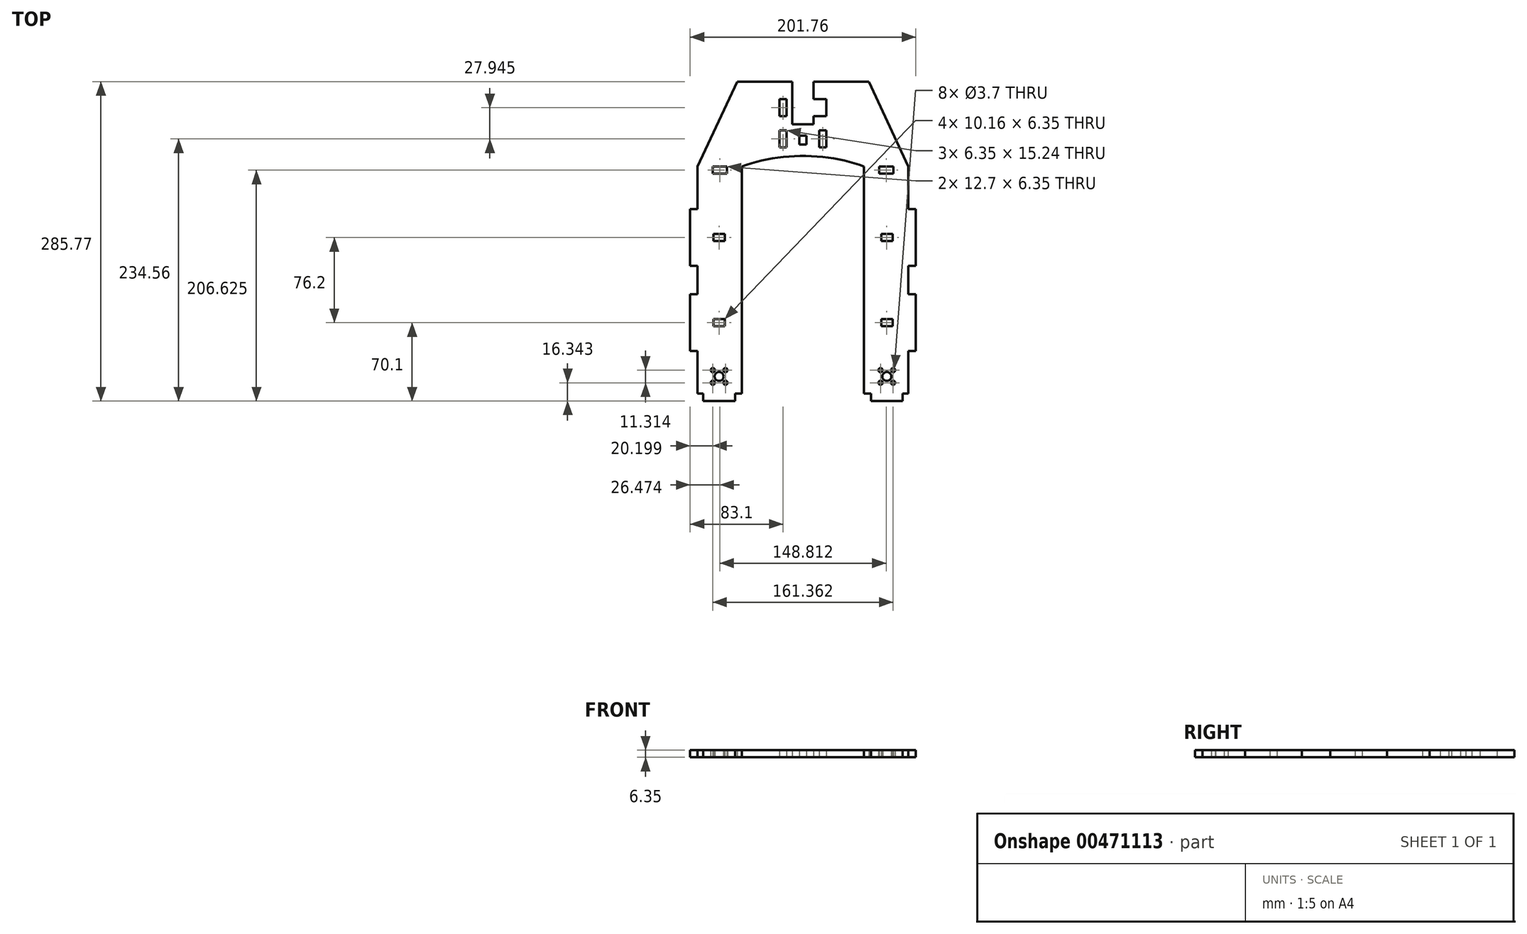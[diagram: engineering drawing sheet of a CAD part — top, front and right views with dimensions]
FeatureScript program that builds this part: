
annotation { "Feature Type Name" : "Feature", "Feature Type Description" : "" }
export const myFeature = defineFeature(function(context is Context, id is Id, definition is map)
    precondition{}
    {
        {
            var Q0;
            Q0=qCreatedBy(makeId("Top.planeOp"),FACE);
            var sketch = newSketch(context, id + "F0", { "sketchPlane" : qUnion([Q0])});
            skLineSegment(sketch, "E0", {"start": v(-60.85, 0) * mm, "end": v(-60.85, -6.6) * mm});
            skLineSegment(sketch, "E1", {"start": v(-60.85, -6.6) * mm, "end": v(-89.2, -6.6) * mm});
            skLineSegment(sketch, "E2", {"start": v(-89.2, -6.6) * mm, "end": v(-89.2, 0) * mm});
            skLineSegment(sketch, "E3", {"start": v(-89.2, 0) * mm, "end": v(-94.28, 0) * mm});
            skLineSegment(sketch, "E4", {"start": v(-60.85, 0) * mm, "end": v(-54.53, 0) * mm});
            skLineSegment(sketch, "E5", {"start": v(-94.28, 0) * mm, "end": v(-94.28, 38.1) * mm});
            skLineSegment(sketch, "E6", {"start": v(-54.53, 0) * mm, "end": v(-54.53, 203.2) * mm});
            skFitSpline(sketch, "E7", {"points": [v(-54.53, 203.2) * mm, v(54.53, 203.2) * mm], "startDerivative": vector(94.5, 38.1) * mm, "endDerivative": vector(94.5, -38.1) * mm});
            skLineSegment(sketch, "E8", {"start": v(-94.28, 38.1) * mm, "end": v(-100.88, 38.1) * mm});
            skLineSegment(sketch, "E9", {"start": v(-100.88, 38.1) * mm, "end": v(-100.88, 88.9) * mm});
            skLineSegment(sketch, "E10", {"start": v(-100.88, 88.9) * mm, "end": v(-94.28, 88.9) * mm});
            skLineSegment(sketch, "E11", {"start": v(-94.28, 165.1) * mm, "end": v(-100.88, 165.1) * mm});
            skLineSegment(sketch, "E12", {"start": v(-100.88, 165.1) * mm, "end": v(-100.88, 114.3) * mm});
            skLineSegment(sketch, "E13", {"start": v(-100.88, 114.3) * mm, "end": v(-94.28, 114.3) * mm});
            skLineSegment(sketch, "E14.trimOffspring", {"start": v(-94.28, 165.1) * mm, "end": v(-94.28, 203.2) * mm});
            skLineSegment(sketch, "E15.trimOffspring", {"start": v(-94.28, 88.9) * mm, "end": v(-94.28, 114.3) * mm});
            skCircle(sketch, "E16", {"center": v(-75.02, 15.4) * mm, "radius": 4 * mm});
            skCircle(sketch, "E17.1.0", {"center": v(-80.68, 9.74) * mm, "radius": 1.85 * mm});
            skCircle(sketch, "E18.1.3.0", {"center": v(-69.37, 9.74) * mm, "radius": 1.85 * mm});
            skCircle(sketch, "E18.1.5.0", {"center": v(-69.37, 21.06) * mm, "radius": 1.85 * mm});
            skCircle(sketch, "E18.1.7.0", {"center": v(-80.68, 21.06) * mm, "radius": 1.85 * mm});
            skLineSegment(sketch, "E19", {"start": v(-80.76, 203.2) * mm, "end": v(-80.76, 196.85) * mm});
            skLineSegment(sketch, "E20", {"start": v(-80.76, 196.85) * mm, "end": v(-68.06, 196.85) * mm});
            skLineSegment(sketch, "E21", {"start": v(-68.06, 196.85) * mm, "end": v(-68.06, 203.2) * mm});
            skLineSegment(sketch, "E22", {"start": v(-80.76, 203.2) * mm, "end": v(-68.06, 203.2) * mm});
            skLineSegment(sketch, "E23", {"start": v(0, 0) * mm, "end": v(0, 212.73) * mm, "construction": true});
            skLineSegment(sketch, "E24", {"start": v(-58.85, 279.17) * mm, "end": v(-9.53, 279.17) * mm});
            skLineSegment(sketch, "E25", {"start": v(-94.28, 203.2) * mm, "end": v(-58.85, 279.17) * mm});
            skLineSegment(sketch, "E26", {"start": v(-9.53, 279.17) * mm, "end": v(-9.53, 241.07) * mm});
            skLineSegment(sketch, "E27.MirrorCS", {"start": v(94.28, 203.2) * mm, "end": v(58.85, 279.17) * mm});
            skLineSegment(sketch, "E28.MirrorCS", {"start": v(9.53, 279.17) * mm, "end": v(9.53, 263.53) * mm});
            skLineSegment(sketch, "E29.MirrorCS", {"start": v(58.85, 279.17) * mm, "end": v(9.53, 279.17) * mm});
            skLineSegment(sketch, "E30.MirrorCS", {"start": v(80.76, 203.2) * mm, "end": v(80.76, 196.85) * mm});
            skCircle(sketch, "E31.MirrorC", {"center": v(69.37, 9.74) * mm, "radius": 1.85 * mm});
            skCircle(sketch, "E32.MirrorC", {"center": v(69.37, 21.06) * mm, "radius": 1.85 * mm});
            skLineSegment(sketch, "E33.MirrorCS", {"start": v(80.76, 196.85) * mm, "end": v(68.06, 196.85) * mm});
            skLineSegment(sketch, "E34.MirrorCS", {"start": v(100.88, 114.3) * mm, "end": v(94.28, 114.3) * mm});
            skCircle(sketch, "E35.MirrorC", {"center": v(75.02, 15.4) * mm, "radius": 4 * mm});
            skLineSegment(sketch, "E36.MirrorCS", {"start": v(89.2, -6.6) * mm, "end": v(89.2, 0) * mm});
            skLineSegment(sketch, "E37.MirrorCS", {"start": v(60.85, 0) * mm, "end": v(60.85, -6.6) * mm});
            skLineSegment(sketch, "E38.MirrorCS", {"start": v(60.85, 0) * mm, "end": v(54.53, 0) * mm});
            skLineSegment(sketch, "E39.MirrorCS", {"start": v(80.76, 203.2) * mm, "end": v(68.06, 203.2) * mm});
            skLineSegment(sketch, "E40.MirrorCS", {"start": v(94.28, 38.1) * mm, "end": v(100.88, 38.1) * mm});
            skLineSegment(sketch, "E41.MirrorCS", {"start": v(100.88, 88.9) * mm, "end": v(94.28, 88.9) * mm});
            skLineSegment(sketch, "E42.MirrorCS", {"start": v(94.28, 165.1) * mm, "end": v(100.88, 165.1) * mm});
            skLineSegment(sketch, "E43.MirrorCS", {"start": v(68.06, 196.85) * mm, "end": v(68.06, 203.2) * mm});
            skLineSegment(sketch, "E44.MirrorCS", {"start": v(89.2, 0) * mm, "end": v(94.28, 0) * mm});
            skCircle(sketch, "E45.MirrorC", {"center": v(80.68, 9.74) * mm, "radius": 1.85 * mm});
            skCircle(sketch, "E46.MirrorC", {"center": v(80.68, 21.06) * mm, "radius": 1.85 * mm});
            skLineSegment(sketch, "E47.MirrorCS", {"start": v(60.85, -6.6) * mm, "end": v(89.2, -6.6) * mm});
            skLineSegment(sketch, "E48.MirrorCS", {"start": v(94.28, 165.1) * mm, "end": v(94.28, 203.2) * mm});
            skLineSegment(sketch, "E49.MirrorCS", {"start": v(94.28, 88.9) * mm, "end": v(94.28, 114.3) * mm});
            skLineSegment(sketch, "E50.MirrorCS", {"start": v(94.28, 0) * mm, "end": v(94.28, 38.1) * mm});
            skLineSegment(sketch, "E51.MirrorCS", {"start": v(54.53, 0) * mm, "end": v(54.53, 203.2) * mm});
            skLineSegment(sketch, "E52.MirrorCS", {"start": v(100.88, 38.1) * mm, "end": v(100.88, 88.9) * mm});
            skLineSegment(sketch, "E53.MirrorCS", {"start": v(100.88, 165.1) * mm, "end": v(100.88, 114.3) * mm});
            skLineSegment(sketch, "E54", {"start": v(-9.53, 241.07) * mm, "end": v(9.53, 241.07) * mm});
            skLineSegment(sketch, "E55", {"start": v(14.6, 235.58) * mm, "end": v(20.96, 235.58) * mm});
            skLineSegment(sketch, "E56", {"start": v(20.96, 235.58) * mm, "end": v(20.96, 220.34) * mm});
            skLineSegment(sketch, "E57", {"start": v(20.96, 220.34) * mm, "end": v(14.6, 220.34) * mm});
            skLineSegment(sketch, "E58", {"start": v(14.6, 220.34) * mm, "end": v(14.6, 235.58) * mm});
            skLineSegment(sketch, "E59", {"start": v(20.96, 263.53) * mm, "end": v(20.96, 248.29) * mm});
            skLineSegment(sketch, "E60.MirrorCS", {"start": v(-20.96, 235.58) * mm, "end": v(-20.96, 220.34) * mm});
            skLineSegment(sketch, "E61.MirrorCS", {"start": v(-14.6, 235.58) * mm, "end": v(-20.96, 235.58) * mm});
            skLineSegment(sketch, "E62.MirrorCS", {"start": v(-20.96, 220.34) * mm, "end": v(-14.6, 220.34) * mm});
            skLineSegment(sketch, "E63.MirrorCS", {"start": v(-20.96, 248.29) * mm, "end": v(-14.6, 248.29) * mm});
            skLineSegment(sketch, "E64.MirrorCS", {"start": v(-14.6, 220.34) * mm, "end": v(-14.6, 235.58) * mm});
            skLineSegment(sketch, "E65.MirrorCS", {"start": v(-14.6, 248.29) * mm, "end": v(-14.6, 263.53) * mm});
            skLineSegment(sketch, "E66.MirrorCS", {"start": v(-14.6, 263.53) * mm, "end": v(-20.96, 263.53) * mm});
            skLineSegment(sketch, "E67.MirrorCS", {"start": v(-20.96, 263.53) * mm, "end": v(-20.96, 248.29) * mm});
            skLineSegment(sketch, "E68.trimOffspring", {"start": v(9.53, 248.29) * mm, "end": v(9.53, 241.07) * mm});
            skLineSegment(sketch, "E69", {"start": v(9.53, 263.53) * mm, "end": v(20.96, 263.53) * mm});
            skLineSegment(sketch, "E70", {"start": v(9.53, 248.29) * mm, "end": v(20.96, 248.29) * mm});
            skPoint(sketch, "E71.endSnap0", {"position": v(0, 241.07) * mm});
            skLineSegment(sketch, "E72", {"start": v(3.18, 230.9) * mm, "end": v(3.18, 222.89) * mm});
            skLineSegment(sketch, "E73.MirrorCS", {"start": v(-3.18, 230.9) * mm, "end": v(-3.18, 222.89) * mm});
            skLineSegment(sketch, "E74", {"start": v(-3.18, 222.89) * mm, "end": v(3.18, 222.89) * mm});
            skLineSegment(sketch, "E75", {"start": v(-3.18, 230.9) * mm, "end": v(3.18, 230.9) * mm});
            skLineSegment(sketch, "E76", {"start": v(54.53, 0) * mm, "end": v(-54.53, 0) * mm, "construction": true});
            skLineSegment(sketch, "E77", {"start": v(-75.02, 15.4) * mm, "end": v(-75.02, 174.62) * mm, "construction": true});
            skLineSegment(sketch, "E78", {"start": v(-100.88, 139.7) * mm, "end": v(-54.53, 139.7) * mm, "construction": true});
            skLineSegment(sketch, "E79", {"start": v(-80.1, 142.88) * mm, "end": v(-69.94, 142.88) * mm});
            skLineSegment(sketch, "E80.MirrorCS", {"start": v(-80.1, 136.53) * mm, "end": v(-69.94, 136.53) * mm});
            skLineSegment(sketch, "E81", {"start": v(-80.1, 142.88) * mm, "end": v(-80.1, 136.53) * mm});
            skLineSegment(sketch, "E82", {"start": v(-69.94, 142.88) * mm, "end": v(-69.94, 136.53) * mm});
            skLineSegment(sketch, "E83", {"start": v(-94.28, 101.6) * mm, "end": v(-54.53, 101.6) * mm, "construction": true});
            skLineSegment(sketch, "E84.MirrorCS", {"start": v(-80.1, 66.68) * mm, "end": v(-69.94, 66.68) * mm});
            skLineSegment(sketch, "E85.MirrorCS", {"start": v(-80.1, 60.33) * mm, "end": v(-69.94, 60.33) * mm});
            skLineSegment(sketch, "E86.MirrorCS", {"start": v(-69.94, 60.32) * mm, "end": v(-69.94, 66.68) * mm});
            skLineSegment(sketch, "E87.MirrorCS", {"start": v(-80.1, 60.32) * mm, "end": v(-80.1, 66.68) * mm});
            skLineSegment(sketch, "E88.MirrorCS", {"start": v(80.1, 142.88) * mm, "end": v(69.94, 142.88) * mm});
            skLineSegment(sketch, "E89.MirrorCS", {"start": v(80.1, 142.88) * mm, "end": v(80.1, 136.53) * mm});
            skLineSegment(sketch, "E90.MirrorCS", {"start": v(80.1, 136.53) * mm, "end": v(69.94, 136.53) * mm});
            skLineSegment(sketch, "E91.MirrorCS", {"start": v(69.94, 142.88) * mm, "end": v(69.94, 136.53) * mm});
            skLineSegment(sketch, "E92.MirrorCS", {"start": v(80.1, 66.68) * mm, "end": v(69.94, 66.68) * mm});
            skLineSegment(sketch, "E93.MirrorCS", {"start": v(69.94, 60.32) * mm, "end": v(69.94, 66.68) * mm});
            skLineSegment(sketch, "E94.MirrorCS", {"start": v(80.1, 60.33) * mm, "end": v(69.94, 60.33) * mm});
            skLineSegment(sketch, "E95.MirrorCS", {"start": v(80.1, 60.32) * mm, "end": v(80.1, 66.68) * mm});
            skSolve(sketch);
        }
        {
            var Q0;
            Q0=makeQuery(id+"F0.imprint","IMPRINT",FACE,{"disambiguationData":[TD([[makeQuery(id+"F0.imprint","IMPRINT",EDGE,{"derivedFrom":sQuery(id+"F0.wireOp",EDGE,"E0")}),-1.0]])]});
            extrude(context, id + "F1", {"entities" : qUnion([Q0]), "depth" : 6.35 * mm});
        }
    });
